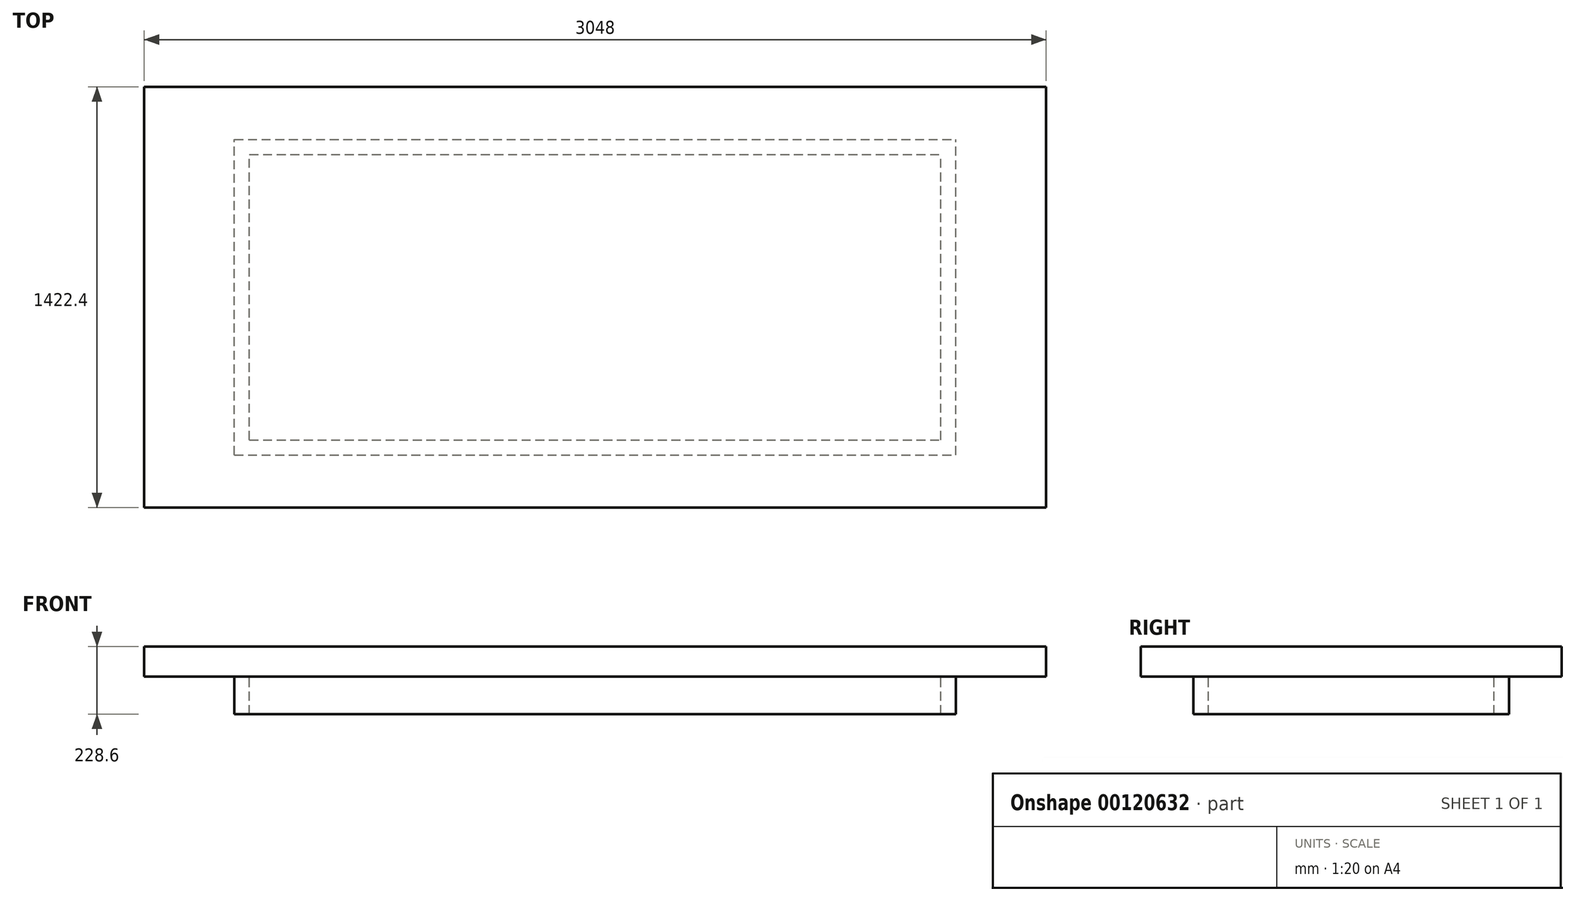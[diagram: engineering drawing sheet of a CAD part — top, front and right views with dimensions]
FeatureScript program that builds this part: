
annotation { "Feature Type Name" : "Feature", "Feature Type Description" : "" }
export const myFeature = defineFeature(function(context is Context, id is Id, definition is map)
    precondition{}
    {
        {
            var Q0;
            Q0=qCreatedBy(makeId("Top.planeOp"),FACE);
            var sketch = newSketch(context, id + "F0", { "sketchPlane" : qUnion([Q0])});
            skLineSegment(sketch, "E0.bottom", {"start": v(-1524, 711.2) * mm, "end": v(1524, 711.2) * mm});
            skLineSegment(sketch, "E0.top", {"start": v(-1524, -711.2) * mm, "end": v(1524, -711.2) * mm});
            skLineSegment(sketch, "E0.left", {"start": v(-1524, 711.2) * mm, "end": v(-1524, -711.2) * mm});
            skLineSegment(sketch, "E0.right", {"start": v(1524, 711.2) * mm, "end": v(1524, -711.2) * mm});
            skPoint(sketch, "E0.middle", {"position": v(0, 0) * mm});
            skSolve(sketch);
        }
        {
            var Q0;
            Q0 = qSketchRegion(id + "F0", true);
            extrude(context, id + "F1", {"entities" : qUnion([Q0]), "depth" : 101.6 * mm});
        }
        {
            var Q0;
            Q0=makeQuery(id+"F1.opExtrude","CAP_FACE",FACE,{"disambiguationData":[OSD([sQuery(id+"F0.wireOp",EDGE,"E0.bottom"),sQuery(id+"F0.wireOp",EDGE,"E0.top"),sQuery(id+"F0.wireOp",EDGE,"E0.left"),sQuery(id+"F0.wireOp",EDGE,"E0.right")])],"isStart":true});
            var sketch = newSketch(context, id + "F2", { "sketchPlane" : qUnion([Q0])});
            skLineSegment(sketch, "E1.bottom", {"start": v(-1219.2, 533.4) * mm, "end": v(1219.2, 533.4) * mm});
            skLineSegment(sketch, "E1.top", {"start": v(-1219.2, -533.4) * mm, "end": v(1219.2, -533.4) * mm});
            skLineSegment(sketch, "E1.left", {"start": v(-1219.2, 533.4) * mm, "end": v(-1219.2, -533.4) * mm});
            skLineSegment(sketch, "E1.right", {"start": v(1219.2, 533.4) * mm, "end": v(1219.2, -533.4) * mm});
            skPoint(sketch, "E1.middle", {"position": v(0, 0) * mm});
            skLineSegment(sketch, "E2.bottom", {"start": v(-1168.4, 482.6) * mm, "end": v(1168.4, 482.6) * mm});
            skLineSegment(sketch, "E2.top", {"start": v(-1168.4, -482.6) * mm, "end": v(1168.4, -482.6) * mm});
            skLineSegment(sketch, "E2.left", {"start": v(-1168.4, 482.6) * mm, "end": v(-1168.4, -482.6) * mm});
            skLineSegment(sketch, "E2.right", {"start": v(1168.4, 482.6) * mm, "end": v(1168.4, -482.6) * mm});
            skSolve(sketch);
        }
        {
            var Q0;
            Q0=makeQuery(id+"F2.imprint","IMPRINT",FACE,{"disambiguationData":[TD([[makeQuery(id+"F2.imprint","IMPRINT",EDGE,{"derivedFrom":sQuery(id+"F2.wireOp",EDGE,"E1.bottom")}),-1.0]])]});
            extrude(context, id + "F3", {"entities" : qUnion([Q0]), "operationType" : NewBodyOperationType.ADD, "depth" : 127 * mm});
        }
    });
